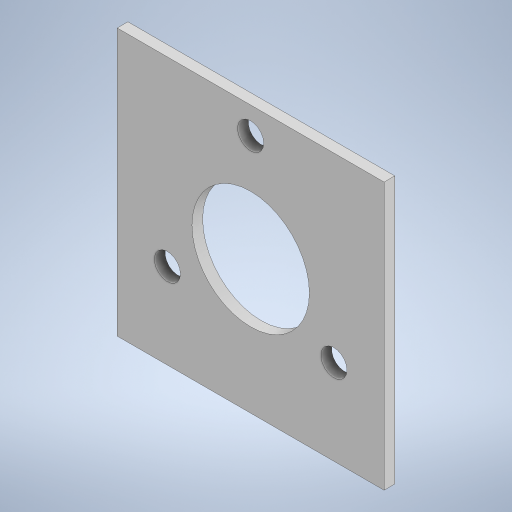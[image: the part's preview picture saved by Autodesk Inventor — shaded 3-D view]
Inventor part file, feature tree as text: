
AUTODESK INVENTOR PART (.ipt)
format: ipt  version: 2024 (Build 280153000, 153)  size: 235,008 bytes
history: native  units: in
note: dims shown in document units (in); Inventor stores cm internally (conversion verified against a paired STEP export)
features: extrude x1, sketch x1
ambient origin geometry x8: Origin, YZ Plane, XZ Plane, XY Plane, X Axis, Y Axis, Z Axis, Center Point
bodies: Body1 (feature_tree)
feature tree (2):
  extrude  "Extrusion2"  Depth=1.9685in
  sketch  "Sketch1"  dims[d0=1.9685in d1=1.9685in d2=0.8661in d3=0.7874in d4=0.6142in d5=120.0deg d6=0.6142in d7=120.0deg d8=0.1929in d9=0.1929in d10=0.1929in d16=0.0787in d17=0.0in d11=0.0197in d12=0.0344in d13=0.0197in d14=0.0344in]
